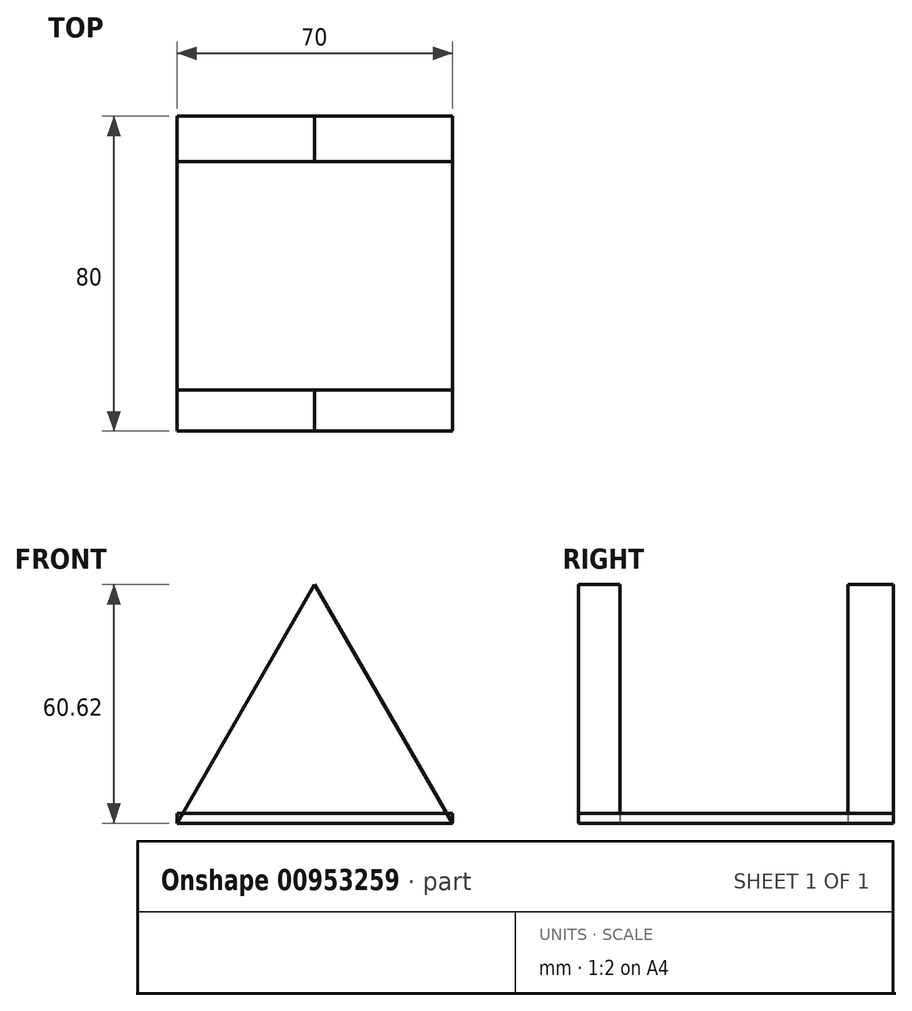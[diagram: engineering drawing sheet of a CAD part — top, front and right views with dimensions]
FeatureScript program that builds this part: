
annotation { "Feature Type Name" : "Feature", "Feature Type Description" : "" }
export const myFeature = defineFeature(function(context is Context, id is Id, definition is map)
    precondition{}
    {
        {
            var Q0;
            Q0=qCreatedBy(makeId("Front.planeOp"),FACE);
            var sketch = newSketch(context, id + "F0", { "sketchPlane" : qUnion([Q0])});
            skLineSegment(sketch, "E0", {"start": v(0, 60.62) * mm, "end": v(-35, 0) * mm});
            skLineSegment(sketch, "E1", {"start": v(-35, 0) * mm, "end": v(35, 0) * mm});
            skLineSegment(sketch, "E2", {"start": v(35, 0) * mm, "end": v(0, 60.62) * mm});
            skSolve(sketch);
        }
        {
            var Q0;
            Q0 = qSketchRegion(id + "F0", true);
            extrude(context, id + "F1", {"entities" : qUnion([Q0]), "depth" : 80 * mm, "offsetDistance" : 25 * mm});
        }
        {
            var Q0;
            Q0=makeQuery(id+"F1.opExtrude","SWEPT_FACE",FACE,{"disambiguationData":[OSD([sQuery(id+"F0.wireOp",EDGE,"E0")])]});
            var sketch = newSketch(context, id + "F2", { "sketchPlane" : qUnion([Q0])});
            skLineSegment(sketch, "E3.bottom", {"start": v(11.52, 52.5) * mm, "end": v(69.5, 52.5) * mm});
            skLineSegment(sketch, "E3.top", {"start": v(11.52, -17.5) * mm, "end": v(69.5, -17.5) * mm});
            skLineSegment(sketch, "E3.left", {"start": v(11.52, 52.5) * mm, "end": v(11.52, -17.5) * mm});
            skLineSegment(sketch, "E3.right", {"start": v(69.5, 52.5) * mm, "end": v(69.5, -17.5) * mm});
            skSolve(sketch);
        }
        {
            var Q0;
            Q0 = qSketchRegion(id + "F2", true);
            extrude(context, id + "F3", {"entities" : qUnion([Q0]), "operationType" : NewBodyOperationType.REMOVE, "oppositeDirection" : true, "depth" : 100 * mm, "offsetDistance" : 25 * mm});
        }
        {
            var Q0;
            Q0=qCreatedBy(makeId("Top.planeOp"),FACE);
            var sketch = newSketch(context, id + "F4", { "sketchPlane" : qUnion([Q0])});
            skLineSegment(sketch, "E4.bottom", {"start": v(-35, 0) * mm, "end": v(35, 0) * mm});
            skLineSegment(sketch, "E4.top", {"start": v(-35, -80) * mm, "end": v(35, -80) * mm});
            skLineSegment(sketch, "E4.left", {"start": v(-35, 0) * mm, "end": v(-35, -80) * mm});
            skLineSegment(sketch, "E4.right", {"start": v(35, 0) * mm, "end": v(35, -80) * mm});
            skSolve(sketch);
        }
        {
            var Q0;
            Q0 = qSketchRegion(id + "F4", true);
            extrude(context, id + "F5", {"entities" : qUnion([Q0]), "depth" : 2.5 * mm, "offsetDistance" : 25 * mm});
        }
    });
